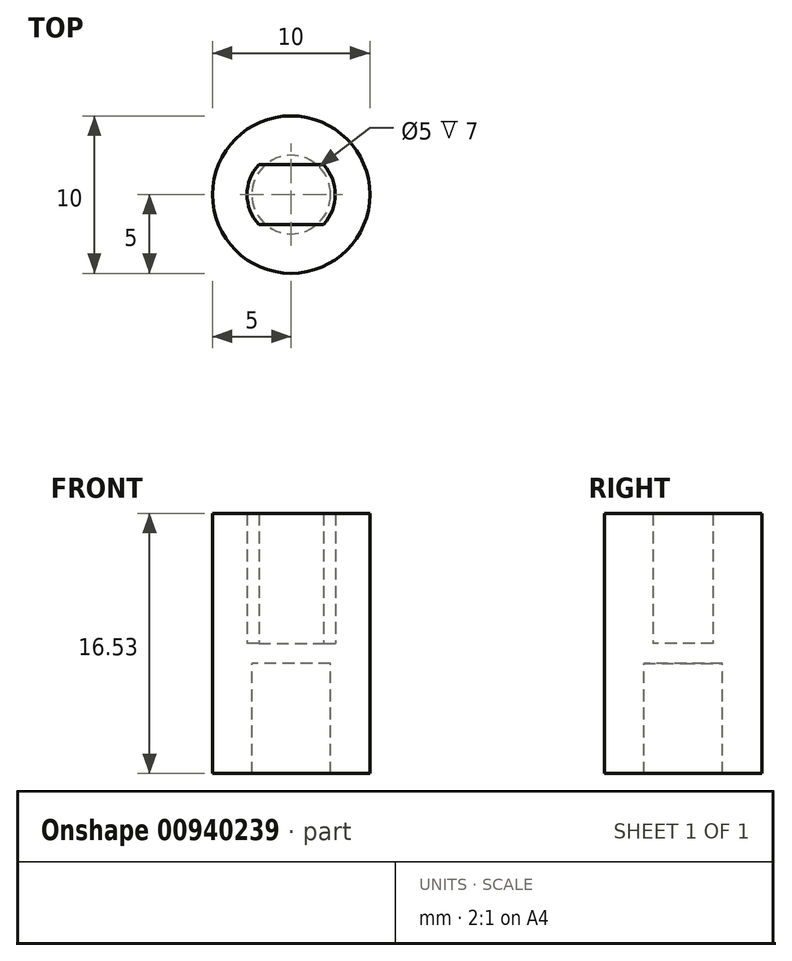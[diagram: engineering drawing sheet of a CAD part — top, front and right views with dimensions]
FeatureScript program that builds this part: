
annotation { "Feature Type Name" : "Feature", "Feature Type Description" : "" }
export const myFeature = defineFeature(function(context is Context, id is Id, definition is map)
    precondition{}
    {
        {
            var Q0;
            Q0=qCreatedBy(makeId("Top.planeOp"),FACE);
            var sketch = newSketch(context, id + "F0", { "sketchPlane" : qUnion([Q0])});
            skCircle(sketch, "E0", {"center": v(0, 0) * mm, "radius": 5 * mm});
            skSolve(sketch);
        }
        {
            var Q0;
            Q0 = qSketchRegion(id + "F0", true);
            extrude(context, id + "F1", {"entities" : qUnion([Q0]), "depth" : 9.52 * mm, "offsetDistance" : 25.4 * mm, "hasSecondDirection" : true, "secondDirectionOppositeDirection" : true, "secondDirectionDepth" : 7 * mm});
        }
        {
            var Q0;
            Q0=qCreatedBy(makeId("Top.planeOp"),FACE);
            var sketch = newSketch(context, id + "F2", { "sketchPlane" : qUnion([Q0])});
            skCircle(sketch, "E1", {"center": v(0, 0) * mm, "radius": 2.8 * mm});
            skLineSegment(sketch, "E2", {"start": v(-2.06, 1.9) * mm, "end": v(2.06, 1.9) * mm});
            skLineSegment(sketch, "E3", {"start": v(-2.06, -1.9) * mm, "end": v(2.06, -1.9) * mm});
            skSolve(sketch);
        }
        {
            var Q0;
            Q0=qCreatedBy(makeId("Top.planeOp"),FACE);
            var sketch = newSketch(context, id + "F3", { "sketchPlane" : qUnion([Q0])});
            skCircle(sketch, "E4", {"center": v(0, 0) * mm, "radius": 2.5 * mm});
            skSolve(sketch);
        }
        {
            var Q0;
            {var subQ0=sQuery(id+"F2.wireOp",EDGE,"E2");Q0=makeQuery(id+"F2.imprint","IMPRINT",FACE,{"disambiguationData":[TD([[makeQuery(id+"F2.imprint","IMPRINT",EDGE,{"derivedFrom":subQ0}),-1.0]])]});}
            extrude(context, id + "F4", {"entities" : qUnion([Q0]), "operationType" : NewBodyOperationType.REMOVE, "endBound" : BoundingType.THROUGH_ALL, "depth" : 25.4 * mm, "offsetDistance" : 25.4 * mm});
        }
        {
            var Q0;
            Q0 = qSketchRegion(id + "F3", true);
            extrude(context, id + "F5", {"entities" : qUnion([Q0]), "operationType" : NewBodyOperationType.REMOVE, "endBound" : BoundingType.THROUGH_ALL, "oppositeDirection" : true, "depth" : 25.4 * mm, "offsetDistance" : 25.4 * mm});
        }
        {
            var Q0;
            Q0 = qSketchRegion(id + "F0", true);
            extrude(context, id + "F6", {"entities" : qUnion([Q0]), "operationType" : NewBodyOperationType.ADD, "depth" : 1.27 * mm, "offsetDistance" : 25.4 * mm});
        }
    });
